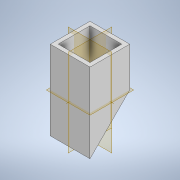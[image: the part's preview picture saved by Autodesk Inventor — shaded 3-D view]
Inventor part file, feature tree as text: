
AUTODESK INVENTOR PART (.ipt)
format: ipt  version: 2022.4 (Build 264492010, 492A)  size: 122,368 bytes
history: native  units: mm
features: extrude x3, sketch x3
ambient origin geometry x8: Origin, YZ Plane, XZ Plane, XY Plane, X Axis, Y Axis, Z Axis, Center Point
bodies: Solid1 (feature_tree)
feature tree (6):
  extrude  "Extrusion1"  Depth=20.0mm
  extrude  "Extrusion2"  Depth=2.0mm
  extrude  "Extrusion3"  Depth=5.0mm
  sketch  "Sketch1"  dims[d0=20.0mm d1=40.0mm]
  sketch  "Sketch2"  dims[d2=20.0mm d3=0.0mm d4=2.0mm]
  sketch  "Sketch3"  dims[d5=20.0mm d6=0.0mm d8=5.0mm d9=5.0mm d10=5.0mm d11=0.0mm]
